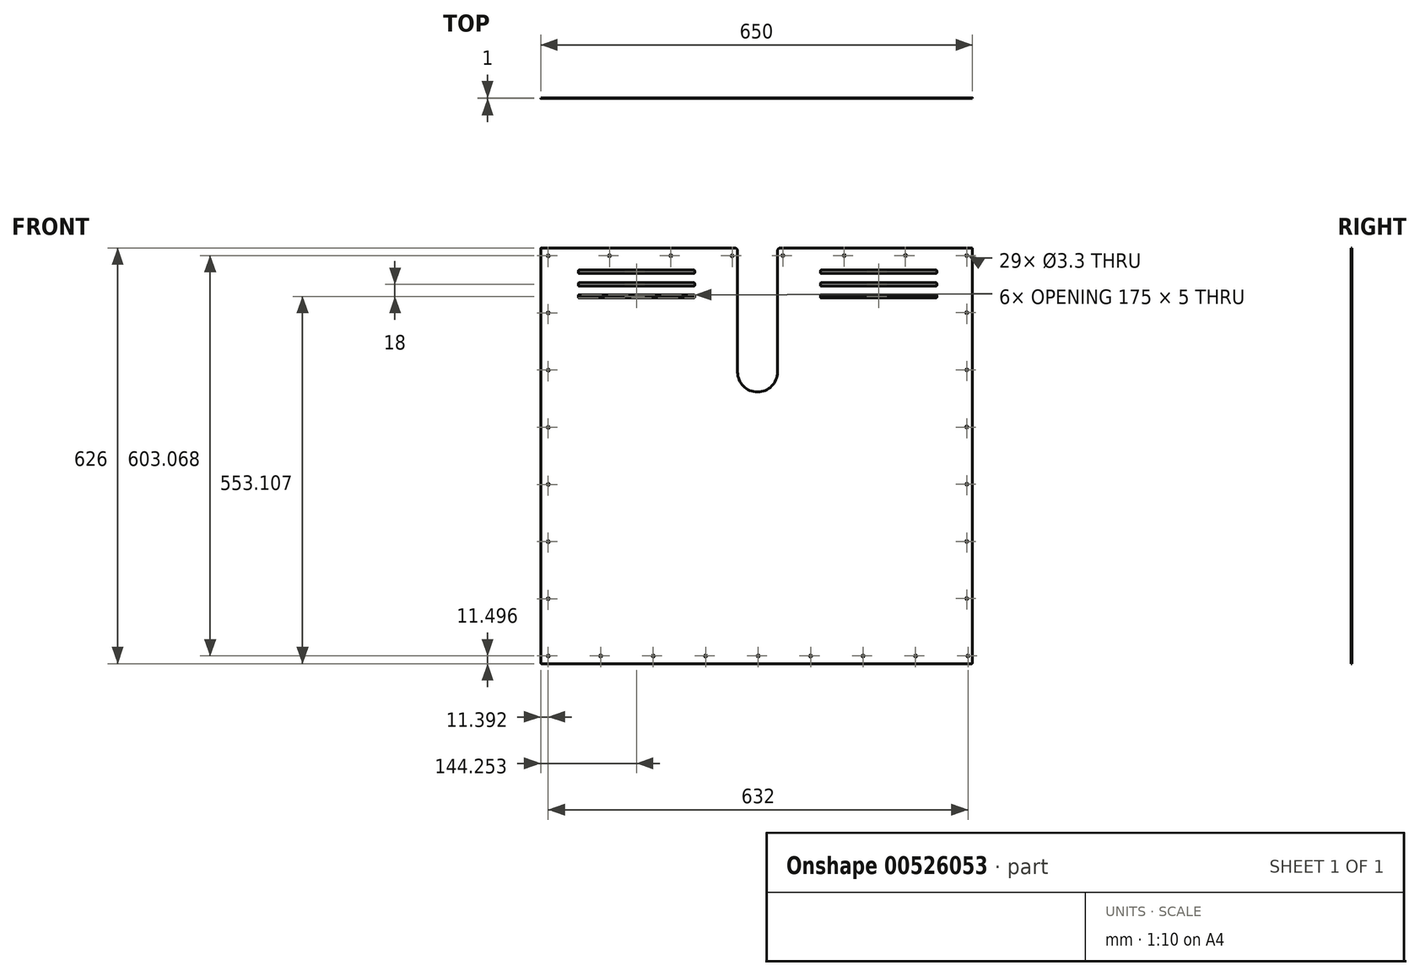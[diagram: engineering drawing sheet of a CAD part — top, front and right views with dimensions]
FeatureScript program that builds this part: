
annotation { "Feature Type Name" : "Feature", "Feature Type Description" : "" }
export const myFeature = defineFeature(function(context is Context, id is Id, definition is map)
    precondition{}
    {
        {
            var Q0;
            Q0=qCreatedBy(makeId("Front.planeOp"),FACE);
            var sketch = newSketch(context, id + "F0", { "sketchPlane" : qUnion([Q0])});
            skArc(sketch, "E0", {"start": v(60.2, 125.02) * mm, "mid": v(90.2, 95.02) * mm, "end": v(120.2, 125.02) * mm});
            skLineSegment(sketch, "E1", {"start": v(120.2, 125.02) * mm, "end": v(120.2, 307.96) * mm});
            skLineSegment(sketch, "E2", {"start": v(60.2, 125.02) * mm, "end": v(60.2, 307.96) * mm});
            skCircle(sketch, "E3", {"center": v(-224.9, 300.16) * mm, "radius": 1.65 * mm});
            skCircle(sketch, "E4.1.0.0", {"center": v(-132.6, 300.16) * mm, "radius": 1.65 * mm});
            skCircle(sketch, "E4.2.0.0", {"center": v(-40.3, 300.16) * mm, "radius": 1.65 * mm});
            skCircle(sketch, "E4.3.0.0", {"center": v(52, 300.16) * mm, "radius": 1.65 * mm});
            skLineSegment(sketch, "E4.direction1", {"start": v(-224.9, 300.16) * mm, "end": v(-132.6, 300.16) * mm, "construction": true});
            skCircle(sketch, "E5.0.1.0", {"center": v(-224.9, 214.06) * mm, "radius": 1.65 * mm});
            skCircle(sketch, "E5.0.2.0", {"center": v(-224.9, 127.96) * mm, "radius": 1.65 * mm});
            skCircle(sketch, "E5.0.3.0", {"center": v(-224.9, 41.86) * mm, "radius": 1.65 * mm});
            skCircle(sketch, "E5.0.4.0", {"center": v(-224.9, -44.24) * mm, "radius": 1.65 * mm});
            skCircle(sketch, "E5.0.5.0", {"center": v(-224.9, -130.34) * mm, "radius": 1.65 * mm});
            skCircle(sketch, "E5.0.6.0", {"center": v(-224.9, -216.44) * mm, "radius": 1.65 * mm});
            skCircle(sketch, "E5.0.7.0", {"center": v(-224.9, -302.54) * mm, "radius": 1.65 * mm});
            skLineSegment(sketch, "E5.direction1", {"start": v(-224.9, 300.16) * mm, "end": v(-199.8, 300.16) * mm, "construction": true});
            skLineSegment(sketch, "E5.direction2", {"start": v(-224.9, 300.16) * mm, "end": v(-224.9, 214.06) * mm, "construction": true});
            skCircle(sketch, "E6.1.0.0", {"center": v(-145.9, -302.54) * mm, "radius": 1.65 * mm});
            skCircle(sketch, "E6.2.0.0", {"center": v(-66.9, -302.54) * mm, "radius": 1.65 * mm});
            skCircle(sketch, "E6.3.0.0", {"center": v(12.1, -302.54) * mm, "radius": 1.65 * mm});
            skCircle(sketch, "E6.4.0.0", {"center": v(91.1, -302.54) * mm, "radius": 1.65 * mm});
            skCircle(sketch, "E6.5.0.0", {"center": v(170.1, -302.54) * mm, "radius": 1.65 * mm});
            skCircle(sketch, "E6.6.0.0", {"center": v(249.1, -302.54) * mm, "radius": 1.65 * mm});
            skCircle(sketch, "E6.7.0.0", {"center": v(328.1, -302.54) * mm, "radius": 1.65 * mm});
            skCircle(sketch, "E6.8.0.0", {"center": v(407.1, -302.54) * mm, "radius": 1.65 * mm});
            skLineSegment(sketch, "E6.direction1", {"start": v(-224.9, -302.54) * mm, "end": v(-145.9, -302.54) * mm, "construction": true});
            skCircle(sketch, "E7", {"center": v(405.26, 300.52) * mm, "radius": 1.65 * mm});
            skCircle(sketch, "E8.0.1.0", {"center": v(405.26, 214.42) * mm, "radius": 1.65 * mm});
            skCircle(sketch, "E8.0.2.0", {"center": v(405.26, 128.32) * mm, "radius": 1.65 * mm});
            skCircle(sketch, "E8.0.3.0", {"center": v(405.26, 42.22) * mm, "radius": 1.65 * mm});
            skCircle(sketch, "E8.0.4.0", {"center": v(405.26, -43.88) * mm, "radius": 1.65 * mm});
            skCircle(sketch, "E8.0.5.0", {"center": v(405.26, -129.98) * mm, "radius": 1.65 * mm});
            skCircle(sketch, "E8.0.6.0", {"center": v(405.26, -216.08) * mm, "radius": 1.65 * mm});
            skLineSegment(sketch, "E8.direction2", {"start": v(405.26, 300.52) * mm, "end": v(405.26, 214.42) * mm, "construction": true});
            skCircle(sketch, "E9.1.0.0", {"center": v(312.96, 300.52) * mm, "radius": 1.65 * mm});
            skCircle(sketch, "E9.2.0.0", {"center": v(220.66, 300.52) * mm, "radius": 1.65 * mm});
            skCircle(sketch, "E9.3.0.0", {"center": v(128.36, 300.52) * mm, "radius": 1.65 * mm});
            skLineSegment(sketch, "E9.direction1", {"start": v(405.26, 300.52) * mm, "end": v(312.96, 300.52) * mm, "construction": true});
            skLineSegment(sketch, "E10.bottom", {"start": v(-178.55, 278.57) * mm, "end": v(-5.55, 278.57) * mm});
            skLineSegment(sketch, "E10.top", {"start": v(-178.55, 273.57) * mm, "end": v(-5.55, 273.57) * mm});
            skLineSegment(sketch, "E10.left", {"start": v(-179.55, 277.57) * mm, "end": v(-179.55, 274.57) * mm});
            skLineSegment(sketch, "E10.right", {"start": v(-4.55, 277.57) * mm, "end": v(-4.55, 274.57) * mm});
            skLineSegment(sketch, "E11.bottom", {"start": v(-178.55, 259.57) * mm, "end": v(-5.55, 259.57) * mm});
            skLineSegment(sketch, "E11.top", {"start": v(-178.55, 254.57) * mm, "end": v(-5.55, 254.57) * mm});
            skLineSegment(sketch, "E11.left", {"start": v(-179.55, 258.57) * mm, "end": v(-179.55, 255.57) * mm});
            skLineSegment(sketch, "E11.right", {"start": v(-4.55, 258.57) * mm, "end": v(-4.55, 255.57) * mm});
            skLineSegment(sketch, "E12.bottom", {"start": v(-178.55, 241.57) * mm, "end": v(-5.55, 241.57) * mm});
            skLineSegment(sketch, "E12.top", {"start": v(-178.55, 236.57) * mm, "end": v(-5.55, 236.57) * mm});
            skLineSegment(sketch, "E12.left", {"start": v(-179.55, 240.57) * mm, "end": v(-179.55, 237.57) * mm});
            skLineSegment(sketch, "E12.right", {"start": v(-4.55, 240.57) * mm, "end": v(-4.55, 237.57) * mm});
            skLineSegment(sketch, "E13.MirrorCS", {"start": v(184.95, 277.57) * mm, "end": v(184.95, 274.57) * mm});
            skLineSegment(sketch, "E14.MirrorCS", {"start": v(184.95, 240.57) * mm, "end": v(184.95, 237.57) * mm});
            skLineSegment(sketch, "E15.MirrorCS", {"start": v(184.95, 258.57) * mm, "end": v(184.95, 255.57) * mm});
            skLineSegment(sketch, "E16.MirrorCS", {"start": v(358.95, 273.57) * mm, "end": v(185.95, 273.57) * mm});
            skLineSegment(sketch, "E17.MirrorCS", {"start": v(358.95, 254.57) * mm, "end": v(185.95, 254.57) * mm});
            skLineSegment(sketch, "E18.MirrorCS", {"start": v(358.95, 278.57) * mm, "end": v(185.95, 278.57) * mm});
            skLineSegment(sketch, "E19.MirrorCS", {"start": v(358.95, 241.57) * mm, "end": v(185.95, 241.57) * mm});
            skLineSegment(sketch, "E20.MirrorCS", {"start": v(358.95, 236.57) * mm, "end": v(185.95, 236.57) * mm});
            skLineSegment(sketch, "E21.MirrorCS", {"start": v(358.95, 259.57) * mm, "end": v(185.95, 259.57) * mm});
            skLineSegment(sketch, "E22", {"start": v(359.95, 277.57) * mm, "end": v(359.95, 274.57) * mm});
            skLineSegment(sketch, "E23", {"start": v(359.95, 258.57) * mm, "end": v(359.95, 255.57) * mm});
            skLineSegment(sketch, "E24", {"start": v(359.95, 240.57) * mm, "end": v(359.95, 237.57) * mm});
            skPoint(sketch, "E25.visualSharp", {"position": v(-4.55, 236.57) * mm});
            skArc(sketch, "E25.filletArc", {"start": v(-5.55, 236.57) * mm, "mid": v(-4.84, 236.86) * mm, "end": v(-4.55, 237.57) * mm});
            skPoint(sketch, "E26.visualSharp", {"position": v(-4.55, 241.57) * mm});
            skArc(sketch, "E26.filletArc", {"start": v(-4.55, 240.57) * mm, "mid": v(-4.84, 241.27) * mm, "end": v(-5.55, 241.57) * mm});
            skPoint(sketch, "E27.visualSharp", {"position": v(-4.55, 254.57) * mm});
            skArc(sketch, "E27.filletArc", {"start": v(-5.55, 254.57) * mm, "mid": v(-4.84, 254.86) * mm, "end": v(-4.55, 255.57) * mm});
            skPoint(sketch, "E28.visualSharp", {"position": v(-4.55, 259.57) * mm});
            skArc(sketch, "E28.filletArc", {"start": v(-4.55, 258.57) * mm, "mid": v(-4.84, 259.27) * mm, "end": v(-5.55, 259.57) * mm});
            skPoint(sketch, "E29.visualSharp", {"position": v(-4.55, 273.57) * mm});
            skArc(sketch, "E29.filletArc", {"start": v(-5.55, 273.57) * mm, "mid": v(-4.84, 273.86) * mm, "end": v(-4.55, 274.57) * mm});
            skPoint(sketch, "E30.visualSharp", {"position": v(-4.55, 278.57) * mm});
            skArc(sketch, "E30.filletArc", {"start": v(-4.55, 277.57) * mm, "mid": v(-4.84, 278.28) * mm, "end": v(-5.55, 278.57) * mm});
            skPoint(sketch, "E31.visualSharp", {"position": v(-179.55, 278.57) * mm});
            skArc(sketch, "E31.filletArc", {"start": v(-178.55, 278.57) * mm, "mid": v(-179.25, 278.28) * mm, "end": v(-179.55, 277.57) * mm});
            skPoint(sketch, "E32.visualSharp", {"position": v(-179.55, 273.57) * mm});
            skArc(sketch, "E32.filletArc", {"start": v(-179.55, 274.57) * mm, "mid": v(-179.25, 273.86) * mm, "end": v(-178.55, 273.57) * mm});
            skPoint(sketch, "E33.visualSharp", {"position": v(-179.55, 259.57) * mm});
            skArc(sketch, "E33.filletArc", {"start": v(-178.55, 259.57) * mm, "mid": v(-179.25, 259.27) * mm, "end": v(-179.55, 258.57) * mm});
            skPoint(sketch, "E34.visualSharp", {"position": v(-179.55, 254.57) * mm});
            skArc(sketch, "E34.filletArc", {"start": v(-179.55, 255.57) * mm, "mid": v(-179.25, 254.86) * mm, "end": v(-178.55, 254.57) * mm});
            skPoint(sketch, "E35.visualSharp", {"position": v(-179.55, 241.57) * mm});
            skArc(sketch, "E35.filletArc", {"start": v(-178.55, 241.57) * mm, "mid": v(-179.25, 241.27) * mm, "end": v(-179.55, 240.57) * mm});
            skPoint(sketch, "E36.visualSharp", {"position": v(-179.55, 236.57) * mm});
            skArc(sketch, "E36.filletArc", {"start": v(-179.55, 237.57) * mm, "mid": v(-179.25, 236.86) * mm, "end": v(-178.55, 236.57) * mm});
            skPoint(sketch, "E37.visualSharp", {"position": v(184.95, 278.57) * mm});
            skArc(sketch, "E37.filletArc", {"start": v(185.95, 278.57) * mm, "mid": v(185.25, 278.28) * mm, "end": v(184.95, 277.57) * mm});
            skPoint(sketch, "E38.visualSharp", {"position": v(184.95, 273.57) * mm});
            skArc(sketch, "E38.filletArc", {"start": v(184.95, 274.57) * mm, "mid": v(185.25, 273.86) * mm, "end": v(185.95, 273.57) * mm});
            skPoint(sketch, "E39.visualSharp", {"position": v(184.95, 259.57) * mm});
            skArc(sketch, "E39.filletArc", {"start": v(185.95, 259.57) * mm, "mid": v(185.25, 259.27) * mm, "end": v(184.95, 258.57) * mm});
            skPoint(sketch, "E40.visualSharp", {"position": v(184.95, 254.57) * mm});
            skArc(sketch, "E40.filletArc", {"start": v(184.95, 255.57) * mm, "mid": v(185.25, 254.86) * mm, "end": v(185.95, 254.57) * mm});
            skPoint(sketch, "E41.visualSharp", {"position": v(184.95, 241.57) * mm});
            skArc(sketch, "E41.filletArc", {"start": v(185.95, 241.57) * mm, "mid": v(185.25, 241.27) * mm, "end": v(184.95, 240.57) * mm});
            skPoint(sketch, "E42.visualSharp", {"position": v(184.95, 236.57) * mm});
            skArc(sketch, "E42.filletArc", {"start": v(184.95, 237.57) * mm, "mid": v(185.25, 236.86) * mm, "end": v(185.95, 236.57) * mm});
            skPoint(sketch, "E43.visualSharp", {"position": v(359.95, 278.57) * mm});
            skArc(sketch, "E43.filletArc", {"start": v(359.95, 277.57) * mm, "mid": v(359.66, 278.28) * mm, "end": v(358.95, 278.57) * mm});
            skPoint(sketch, "E44.visualSharp", {"position": v(359.95, 273.57) * mm});
            skArc(sketch, "E44.filletArc", {"start": v(358.95, 273.57) * mm, "mid": v(359.66, 273.86) * mm, "end": v(359.95, 274.57) * mm});
            skPoint(sketch, "E45.visualSharp", {"position": v(359.95, 259.57) * mm});
            skArc(sketch, "E45.filletArc", {"start": v(359.95, 258.57) * mm, "mid": v(359.66, 259.27) * mm, "end": v(358.95, 259.57) * mm});
            skPoint(sketch, "E46.visualSharp", {"position": v(359.95, 254.57) * mm});
            skArc(sketch, "E46.filletArc", {"start": v(358.95, 254.57) * mm, "mid": v(359.66, 254.86) * mm, "end": v(359.95, 255.57) * mm});
            skPoint(sketch, "E47.visualSharp", {"position": v(359.95, 241.57) * mm});
            skArc(sketch, "E47.filletArc", {"start": v(359.95, 240.57) * mm, "mid": v(359.66, 241.27) * mm, "end": v(358.95, 241.57) * mm});
            skPoint(sketch, "E48.visualSharp", {"position": v(359.95, 236.57) * mm});
            skArc(sketch, "E48.filletArc", {"start": v(358.95, 236.57) * mm, "mid": v(359.66, 236.86) * mm, "end": v(359.95, 237.57) * mm});
            skLineSegment(sketch, "E49.0", {"start": v(-236.3, 310.96) * mm, "end": v(-236.3, -313.04) * mm});
            skLineSegment(sketch, "E50.0", {"start": v(413.7, 310.96) * mm, "end": v(413.7, -313.04) * mm});
            skLineSegment(sketch, "E51.0", {"start": v(-235.3, -314.04) * mm, "end": v(412.7, -314.04) * mm});
            skArc(sketch, "E52.0", {"start": v(-236.3, -313.04) * mm, "mid": v(-236, -313.75) * mm, "end": v(-235.3, -314.04) * mm});
            skArc(sketch, "E53.0", {"start": v(412.7, -314.04) * mm, "mid": v(413.41, -313.75) * mm, "end": v(413.7, -313.04) * mm});
            skLineSegment(sketch, "E54.0", {"start": v(125.2, 311.96) * mm, "end": v(412.7, 311.96) * mm});
            skArc(sketch, "E55.0", {"start": v(413.7, 310.96) * mm, "mid": v(413.41, 311.66) * mm, "end": v(412.7, 311.96) * mm});
            skArc(sketch, "E56", {"start": v(125.2, 311.96) * mm, "mid": v(122, 310.83) * mm, "end": v(120.2, 307.96) * mm});
            skLineSegment(sketch, "E57.0", {"start": v(-235.3, 311.96) * mm, "end": v(55.2, 311.96) * mm});
            skArc(sketch, "E58.MirrorCS", {"start": v(55.2, 311.96) * mm, "mid": v(58.4, 310.83) * mm, "end": v(60.2, 307.96) * mm});
            skArc(sketch, "E59.0", {"start": v(-235.3, 311.96) * mm, "mid": v(-236, 311.66) * mm, "end": v(-236.3, 310.96) * mm});
            skSolve(sketch);
        }
        {
            var Q0;
            Q0=makeQuery(id+"F0.imprint","IMPRINT",FACE,{"disambiguationData":[TD([[makeQuery(id+"F0.imprint","IMPRINT",EDGE,{"derivedFrom":sQuery(id+"F0.wireOp",EDGE,"E0")}),-1.0]])]});
            extrude(context, id + "F1", {"entities" : qUnion([Q0]), "depth" : 1 * mm, "offsetDistance" : 25 * mm});
        }
    });
